# Revit family: PRD_FrankeWS_CntrTopWshBsns_RondoWashbasin_RNDH450-O,RNDX450-O
name_source: partatom
category: Plumbing Fixtures
revit_build: Autodesk Revit 2018 (Build: 20190510_1515(x64)
units: mm (PartAtom-declared; Revit-internal decimal feet)

## family parameters
Cut with Voids When Loaded = No
Host = Face
OmniClass Number = 23.45.05.14.14
OmniClass Title = Sinks/Lavatories
Part Type = Normal
Room Calculation Point = No
Round Connector Dimension = Use Diameter
Shared = No

## types (2) — shared parameters
AssetType = Fixed
Category = Pr_40_20_96_18, Counter top wash basins
Color = Stainless steel
DurationUnit = year
Form = Counter top wash basins
GrossWeight = 3.30 kg
IfcExportAs = IfcSanitaryTerminalType
IfcExportType = WASHHANDBASIN
IntegralAccessories = Lugs for underneath mounting are included
Manufacturer = KWC Group AG
ManufacturerName = KWC Group AG
ManufacturerURL = www.kwc.com
Material = Stainless steel
MaterialsBody = Stainless steel 1.4301
NBSDescription = Counter top wash basins
NBSReference = 45-35-70/360
NetWeight = 3.30 kg
NominalDepth = 392 mm  [stored 1.28609 ft]
NominalHeight = 159 mm  [stored 0.521654 ft]
NominalWidth = 512 mm  [stored 1.67979 ft]
OutcutDiameterTop = 492 x 372 mm
OutcutDiameterUnderneath = 440 x 320 mm
OverflowKit_E-RNDX-UEL-SET = No
ProductInformation = https://pim.kwc.com
Shape = Oval
Size = 512 x 392 x 159 mm
StandardOverflowKit = Yes
URL = www.kwc.com
Uniclass2015Code = Pr_40_20_96_18
Uniclass2015Title = Counter top wash basins
Uniclass2015Version = Products v1.10
Version = 1
WarrantyDurationUnit = year
WashHandBasinMounting = CounterTop
WashHandBasinType = HandRinse
WasteSize = 32  [stored 0.104987 ft]
WaterSupplyOverflowAndWasteHolesOverflow = Yes
WaterSupplyOverflowAndWasteHolesWaste = Center-Back
WaterSupplyOverflowAndWasteHolesWaterSupply = No tapholes
zero-valued in all types: Default Elevation

## per-type parameters (varying)
| type | BIMObjectName | Description | DrainSize | Features | Finish | MaterialsFinishAndColour | Model | ModelNumber | ModelReference | Name | WashbasinMaterial |
| RNDH450-O - High polished | PRD_AR_CounterTopWashBasins_RondoWashbasin_RNDH450-O | Round inset vanity basin, can be mounted from top or underneath, stainless steel, material thickness 1 mm, with overflow, inclusive 5/4" overflow kit without waste, stainless steel lugs for underneath mounting are included.

Surface high-polished
Dimensions 510 x 155 x 390 mm (W x H x D)
Bowl Dimensions 450 x 155 x 330 mm (W x H x D)
Outcut diameter for mounting from top 492 x 372 mm
Outcut diameter for mounting from underneath 440 x 320 mm | DN-32-1-1-4INH | stainless steel, 1.00 mm, high polished, inset mounting, 512x159x392 mm (WxHxD) | High polished | High polished | RNDH450-O | 2000056539 | RNDH450-O | RONDO oval inset vanity basin RNDH450-O | PRD_AR_StainlessSteel_HighPolished |
| RNDX450-O - Satin finished | PRD_AR_CounterTopWashBasins_RondoWashbasin_RNDX450-O | Round inset vanity basin, can be mounted from top or underneath, stainless steel, material thickness 1 mm, with overflow, inclusive 5/4" overflow kit without waste, stainless steel lugs for underneath mounting are included.

Surface satin finished
Dimensions 510 x 155 x 390 mm (W x H x D)
Bowl Dimensions 450 x 155 x 330 mm (W x H x D)
Outcut diameter for mounting from top 492 x 372 mm
Outcut diameter for mounting from underneath 440 x 320 mm | DN 32 (1 1/4 inch.) | stainless steel, 1.00 mm, satin finished, inset mounting, 512x159x392 mm (WxHxD) | Satin finished | Satin finished | RNDX450-O | 2000056606 | RNDX450-O | RONDO oval inset vanity basin RNDX450-O | PRD_AR_StainlessSteel_SatinFinished |

note: [stored X ft] marks values corroborated as IEEE doubles in the binary element streams (Revit-internal decimal feet)

## geometry (parser evidence)
native form markers: Sweep x9
no freeform markers — native parametric forms only
